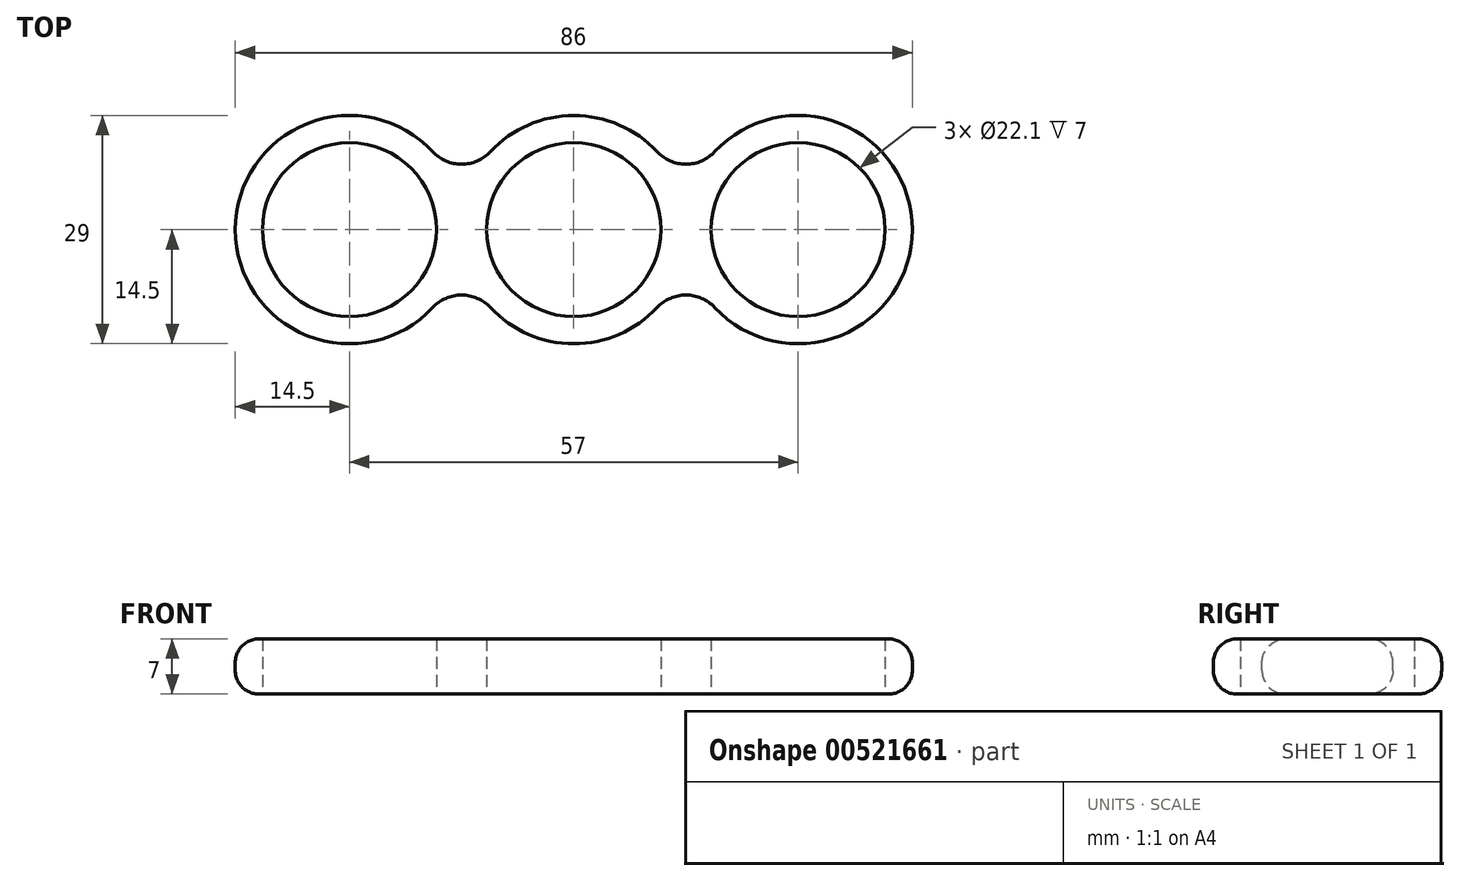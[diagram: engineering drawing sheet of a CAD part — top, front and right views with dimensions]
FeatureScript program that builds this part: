
annotation { "Feature Type Name" : "Feature", "Feature Type Description" : "" }
export const myFeature = defineFeature(function(context is Context, id is Id, definition is map)
    precondition{}
    {
        {
            var Q0;
            Q0=qCreatedBy(makeId("Top.planeOp"),FACE);
            var sketch = newSketch(context, id + "F0", { "sketchPlane" : qUnion([Q0])});
            skCircle(sketch, "E0", {"center": v(0, 0) * mm, "radius": 11.05 * mm});
            skCircle(sketch, "E1", {"center": v(-28.5, 0) * mm, "radius": 11.05 * mm});
            skCircle(sketch, "E2", {"center": v(0, 0) * mm, "radius": 14.5 * mm});
            skCircle(sketch, "E3", {"center": v(-28.5, 0) * mm, "radius": 14.5 * mm});
            skCircle(sketch, "E4.MirrorC", {"center": v(28.5, 0) * mm, "radius": 14.5 * mm});
            skCircle(sketch, "E5.MirrorC", {"center": v(28.5, 0) * mm, "radius": 11.05 * mm});
            skSolve(sketch);
        }
        {
            var Q0;
            {var subQ4=sQuery(id+"F0.wireOp",EDGE,"E1");var subQ7=sQuery(id+"F0.wireOp",EDGE,"ml1K2cT0-D8Ic-48T3-Y5JL-bUitgG3HcKPG");var subQ9=makeQuery(id+"F0.imprint","INTERSECT",VERTEX,{"derivedFrom":[subQ4,subQ7]});Q0=makeQuery(id+"F0.imprint","IMPRINT",FACE,{"disambiguationData":[TD([[makeQuery(id+"F0.imprint","IMPRINT",EDGE,{"disambiguationData":[TD([[subQ9,-1.0]])],"derivedFrom":subQ4}),-1.0]])]});}
            var Q1;
            {var subQ3=sQuery(id+"F0.wireOp",EDGE,"ml1K2cT0-D8Ic-48T3-Y5JL-bUitgG3HcKPG");var subQ5=sQuery(id+"F0.wireOp",EDGE,"E1");var subQ6=makeQuery(id+"F0.imprint","INTERSECT",VERTEX,{"derivedFrom":[subQ5,subQ3]});Q1=makeQuery(id+"F0.imprint","IMPRINT",FACE,{"disambiguationData":[TD([[makeQuery(id+"F0.imprint","IMPRINT",EDGE,{"disambiguationData":[TD([[subQ6,1.0]])],"derivedFrom":subQ5}),-1.0]])]});}
            var Q2;
            {var subQ4=sQuery(id+"F0.wireOp",EDGE,"ml1K2cT0-D8Ic-48T3-Y5JL-bUitgG3HcKPG");var subQ5=sQuery(id+"F0.wireOp",EDGE,"E0");var subQ6=makeQuery(id+"F0.imprint","INTERSECT",VERTEX,{"derivedFrom":[subQ5,subQ4]});Q2=makeQuery(id+"F0.imprint","IMPRINT",FACE,{"disambiguationData":[TD([[makeQuery(id+"F0.imprint","IMPRINT",EDGE,{"disambiguationData":[TD([[subQ6,-1.0]])],"derivedFrom":subQ5}),-1.0]])]});}
            var Q3;
            {var subQ6=sQuery(id+"F0.wireOp",EDGE,"ml1K2cT0-D8Ic-48T3-Y5JL-bUitgG3HcKPG");var subQ7=sQuery(id+"F0.wireOp",EDGE,"E0");var subQ8=makeQuery(id+"F0.imprint","INTERSECT",VERTEX,{"derivedFrom":[subQ7,subQ6]});Q3=makeQuery(id+"F0.imprint","IMPRINT",FACE,{"disambiguationData":[TD([[makeQuery(id+"F0.imprint","IMPRINT",EDGE,{"disambiguationData":[TD([[subQ8,1.0]])],"derivedFrom":subQ7}),-1.0]])]});}
            var Q4;
            {var subQ5=sQuery(id+"F0.wireOp",EDGE,"E4.MirrorC");var subQ6=sQuery(id+"F0.wireOp",EDGE,"E2");var subQ9=makeQuery(id+"F0.imprint","INTERSECT",VERTEX,{"disambiguationData":[OD(0.0)],"derivedFrom":[subQ6,subQ5]});Q4=makeQuery(id+"F0.imprint","IMPRINT",FACE,{"disambiguationData":[TD([[makeQuery(id+"F0.imprint","IMPRINT",EDGE,{"disambiguationData":[TD([[subQ9,1.0]])],"derivedFrom":subQ6}),-1.0]])]});}
            var Q5;
            {var subQ0=sQuery(id+"F0.wireOp",EDGE,"E4.MirrorC");var subQ4=makeQuery(id+"F0.imprint","INTERSECT",VERTEX,{"derivedFrom":[subQ0,sQuery(id+"F0.wireOp",EDGE,"dXiXerwz-CIYk-X3nP-16Fq-8GKO635lf8wP")]});Q5=makeQuery(id+"F0.imprint","IMPRINT",FACE,{"disambiguationData":[TD([[makeQuery(id+"F0.imprint","IMPRINT",EDGE,{"disambiguationData":[TD([[subQ4,1.0]])],"derivedFrom":subQ0}),-1.0]])]});}
            var Q6;
            {var subQ0=sQuery(id+"F0.wireOp",EDGE,"E3");var subQ1=sQuery(id+"F0.wireOp",EDGE,"E2");var subQ2=makeQuery(id+"F0.imprint","INTERSECT",VERTEX,{"disambiguationData":[OD(0.0)],"derivedFrom":[subQ1,subQ0]});Q6=makeQuery(id+"F0.imprint","IMPRINT",FACE,{"disambiguationData":[TD([[makeQuery(id+"F0.imprint","IMPRINT",EDGE,{"disambiguationData":[TD([[subQ2,-1.0]])],"derivedFrom":subQ1}),1.0]])]});}
            var Q7;
            {var subQ0=sQuery(id+"F0.wireOp",EDGE,"E4.MirrorC");var subQ1=sQuery(id+"F0.wireOp",EDGE,"E2");var subQ2=makeQuery(id+"F0.imprint","INTERSECT",VERTEX,{"disambiguationData":[OD(0.0)],"derivedFrom":[subQ1,subQ0]});Q7=makeQuery(id+"F0.imprint","IMPRINT",FACE,{"disambiguationData":[TD([[makeQuery(id+"F0.imprint","IMPRINT",EDGE,{"disambiguationData":[TD([[subQ2,1.0]])],"derivedFrom":subQ1}),1.0]])]});}
            var Q8;
            {var subQ0=sQuery(id+"F0.wireOp",EDGE,"dXiXerwz-CIYk-X3nP-16Fq-8GKO635lf8wP");var subQ1=sQuery(id+"F0.wireOp",EDGE,"E2");var subQ2=makeQuery(id+"F0.imprint","INTERSECT",VERTEX,{"derivedFrom":[subQ1,subQ0]});Q8=makeQuery(id+"F0.imprint","IMPRINT",FACE,{"disambiguationData":[TD([[makeQuery(id+"F0.imprint","IMPRINT",EDGE,{"disambiguationData":[TD([[subQ2,-1.0]])],"derivedFrom":subQ1}),-1.0]])]});}
            var Q9;
            {var subQ0=sQuery(id+"F0.wireOp",EDGE,"E2");var subQ1=makeQuery(id+"F0.imprint","INTERSECT",VERTEX,{"derivedFrom":[subQ0,sQuery(id+"F0.wireOp",EDGE,"dXiXerwz-CIYk-X3nP-16Fq-8GKO635lf8wP")]});Q9=makeQuery(id+"F0.imprint","IMPRINT",FACE,{"disambiguationData":[TD([[makeQuery(id+"F0.imprint","IMPRINT",EDGE,{"disambiguationData":[TD([[subQ1,1.0]])],"derivedFrom":subQ0}),1.0]])]});}
            var Q10;
            {var subQ0=sQuery(id+"F0.wireOp",EDGE,"dXiXerwz-CIYk-X3nP-16Fq-8GKO635lf8wP");var subQ1=sQuery(id+"F0.wireOp",EDGE,"E2");var subQ2=makeQuery(id+"F0.imprint","INTERSECT",VERTEX,{"derivedFrom":[subQ1,subQ0]});Q10=makeQuery(id+"F0.imprint","IMPRINT",FACE,{"disambiguationData":[TD([[makeQuery(id+"F0.imprint","IMPRINT",EDGE,{"disambiguationData":[TD([[subQ2,1.0]])],"derivedFrom":subQ1}),-1.0]])]});}
            var Q11;
            {var subQ0=sQuery(id+"F0.wireOp",EDGE,"xdjUaEcy-FqTV-kRLy-LGmz-1rJnqgSGLtSw");var subQ1=sQuery(id+"F0.wireOp",EDGE,"E2");var subQ2=makeQuery(id+"F0.imprint","INTERSECT",VERTEX,{"derivedFrom":[subQ1,subQ0]});Q11=makeQuery(id+"F0.imprint","IMPRINT",FACE,{"disambiguationData":[TD([[makeQuery(id+"F0.imprint","IMPRINT",EDGE,{"disambiguationData":[TD([[subQ2,-1.0]])],"derivedFrom":subQ1}),-1.0]])]});}
            var Q12;
            {var subQ0=sQuery(id+"F0.wireOp",EDGE,"E2");var subQ1=makeQuery(id+"F0.imprint","INTERSECT",VERTEX,{"derivedFrom":[subQ0,sQuery(id+"F0.wireOp",EDGE,"xdjUaEcy-FqTV-kRLy-LGmz-1rJnqgSGLtSw")]});Q12=makeQuery(id+"F0.imprint","IMPRINT",FACE,{"disambiguationData":[TD([[makeQuery(id+"F0.imprint","IMPRINT",EDGE,{"disambiguationData":[TD([[subQ1,1.0]])],"derivedFrom":subQ0}),1.0]])]});}
            var Q13;
            {var subQ0=sQuery(id+"F0.wireOp",EDGE,"xdjUaEcy-FqTV-kRLy-LGmz-1rJnqgSGLtSw");var subQ1=sQuery(id+"F0.wireOp",EDGE,"E2");var subQ2=makeQuery(id+"F0.imprint","INTERSECT",VERTEX,{"derivedFrom":[subQ1,subQ0]});Q13=makeQuery(id+"F0.imprint","IMPRINT",FACE,{"disambiguationData":[TD([[makeQuery(id+"F0.imprint","IMPRINT",EDGE,{"disambiguationData":[TD([[subQ2,1.0]])],"derivedFrom":subQ1}),-1.0]])]});}
            extrude(context, id + "F1", {"entities" : qUnion([Q0, Q1, Q2, Q3, Q4, Q5, Q6, Q7, Q8, Q9, Q10, Q11, Q12, Q13]), "depth" : 7 * mm, "offsetDistance" : 25 * mm});
        }
        {
            var Q0;
            {var subQ0=sQuery(id+"F0.wireOp",EDGE,"E3");var subQ1=sQuery(id+"F0.wireOp",EDGE,"E2");Q0=makeQuery(id+"F1.opExtrude","SWEPT_EDGE",EDGE,{"disambiguationData":[OSD([subQ1,subQ0]),TDD([makeQuery(id+"F0.imprint","INTERSECT",VERTEX,{"disambiguationData":[OD(1.0)],"derivedFrom":[subQ1,subQ0]})])]});}
            var Q1;
            {var subQ0=sQuery(id+"F0.wireOp",EDGE,"E4.MirrorC");var subQ1=sQuery(id+"F0.wireOp",EDGE,"E2");Q1=makeQuery(id+"F1.opExtrude","SWEPT_EDGE",EDGE,{"disambiguationData":[OSD([subQ1,subQ0]),TDD([makeQuery(id+"F0.imprint","INTERSECT",VERTEX,{"disambiguationData":[OD(1.0)],"derivedFrom":[subQ1,subQ0]})])]});}
            var Q2;
            {var subQ0=sQuery(id+"F0.wireOp",EDGE,"E4.MirrorC");var subQ1=sQuery(id+"F0.wireOp",EDGE,"E2");Q2=makeQuery(id+"F1.opExtrude","SWEPT_EDGE",EDGE,{"disambiguationData":[OSD([subQ1,subQ0]),TDD([makeQuery(id+"F0.imprint","INTERSECT",VERTEX,{"disambiguationData":[OD(0.0)],"derivedFrom":[subQ1,subQ0]})])]});}
            var Q3;
            {var subQ0=sQuery(id+"F0.wireOp",EDGE,"E3");var subQ1=sQuery(id+"F0.wireOp",EDGE,"E2");Q3=makeQuery(id+"F1.opExtrude","SWEPT_EDGE",EDGE,{"disambiguationData":[OSD([subQ1,subQ0]),TDD([makeQuery(id+"F0.imprint","INTERSECT",VERTEX,{"disambiguationData":[OD(0.0)],"derivedFrom":[subQ1,subQ0]})])]});}
            fillet(context, id + "F2", {"entities" : qUnion([Q0, Q1, Q2, Q3]), "radius" : 5 * mm, "tangentPropagation" : true, "allowEdgeOverflow" : false});
        }
        {
            var Q0;
            Q0=makeQuery(id+"F1.opExtrude","CAP_EDGE",EDGE,{"disambiguationData":[OSD([sQuery(id+"F0.wireOp",EDGE,"E4.MirrorC")])],"isStart":false});
            var Q1;
            Q1=makeQuery(id+"F1.opExtrude","CAP_EDGE",EDGE,{"disambiguationData":[OSD([sQuery(id+"F0.wireOp",EDGE,"E4.MirrorC")])],"isStart":true});
            fillet(context, id + "F3", {"entities" : qUnion([Q0, Q1]), "radius" : 3 * mm, "tangentPropagation" : true, "allowEdgeOverflow" : false});
        }
    });
